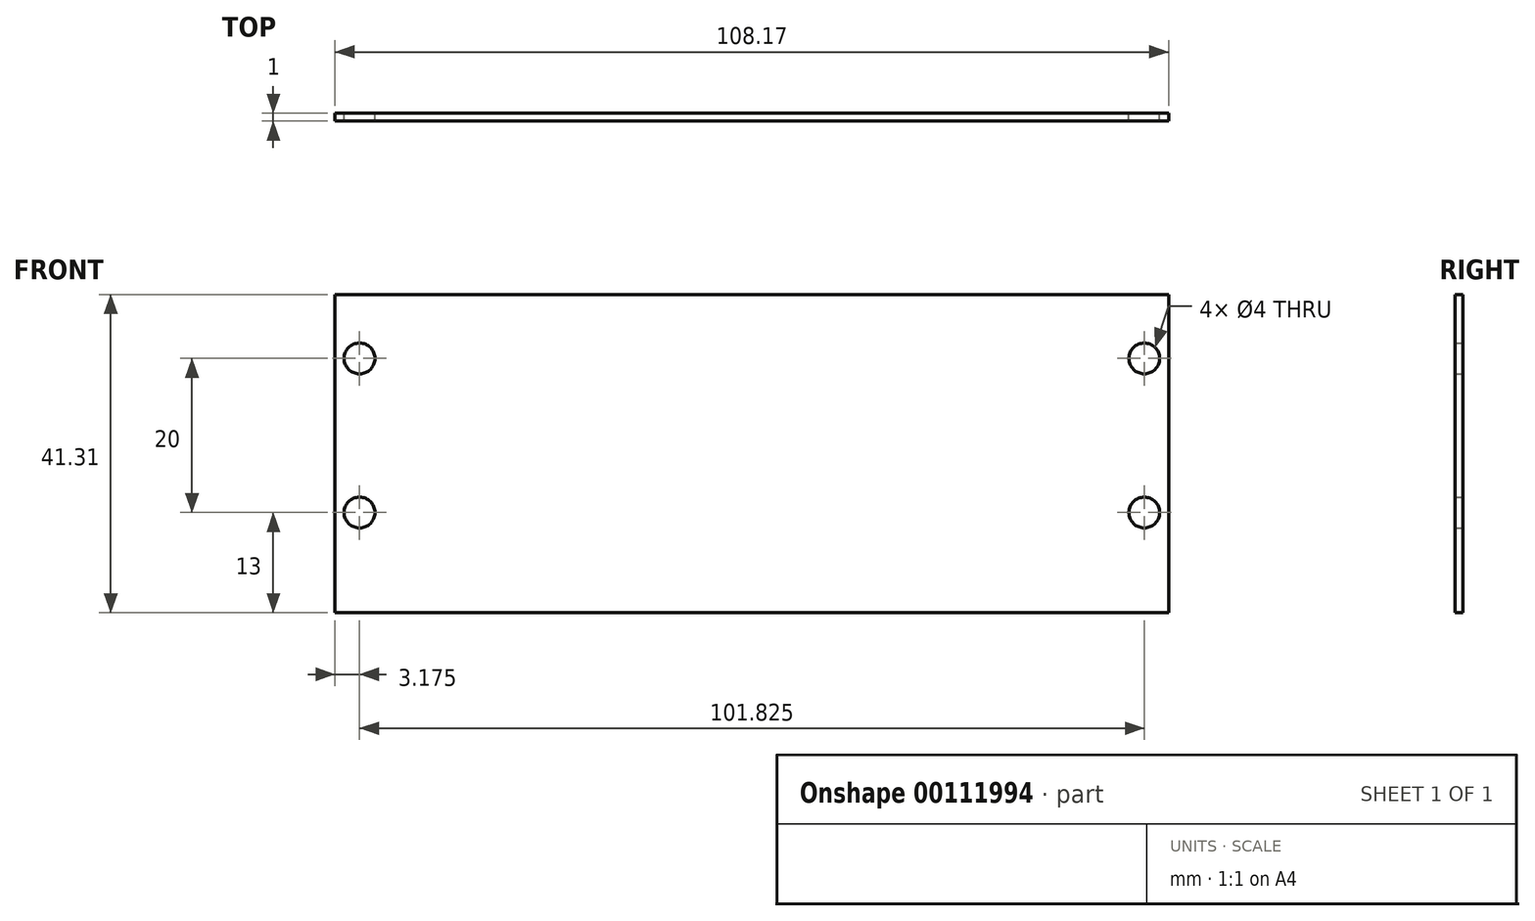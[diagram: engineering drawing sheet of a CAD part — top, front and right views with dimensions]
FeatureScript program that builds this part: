
annotation { "Feature Type Name" : "Feature", "Feature Type Description" : "" }
export const myFeature = defineFeature(function(context is Context, id is Id, definition is map)
    precondition{}
    {
        {
            var Q0;
            Q0=qCreatedBy(makeId("Front.planeOp"),FACE);
            var sketch = newSketch(context, id + "F0", { "sketchPlane" : qUnion([Q0])});
            skLineSegment(sketch, "E0.bottom", {"start": v(0, 0) * mm, "end": v(108.17, 0) * mm});
            skLineSegment(sketch, "E0.top", {"start": v(0, 41.31) * mm, "end": v(108.17, 41.31) * mm});
            skLineSegment(sketch, "E0.left", {"start": v(0, 0) * mm, "end": v(0, 41.31) * mm});
            skLineSegment(sketch, "E0.right", {"start": v(108.17, 0) * mm, "end": v(108.17, 41.31) * mm});
            skLineSegment(sketch, "E1.bottom", {"start": v(3.17, 33) * mm, "end": v(105, 33) * mm, "construction": true});
            skLineSegment(sketch, "E1.top", {"start": v(3.17, 13) * mm, "end": v(105, 13) * mm, "construction": true});
            skLineSegment(sketch, "E1.left", {"start": v(3.17, 33) * mm, "end": v(3.17, 13) * mm, "construction": true});
            skLineSegment(sketch, "E1.right", {"start": v(105, 33) * mm, "end": v(105, 13) * mm, "construction": true});
            skCircle(sketch, "E2", {"center": v(3.17, 33) * mm, "radius": 2 * mm});
            skCircle(sketch, "E3", {"center": v(3.17, 13) * mm, "radius": 2 * mm});
            skCircle(sketch, "E4", {"center": v(105, 13) * mm, "radius": 2 * mm});
            skCircle(sketch, "E5", {"center": v(105, 33) * mm, "radius": 2 * mm});
            skSolve(sketch);
        }
        {
            var Q0;
            Q0 = qSketchRegion(id + "F0", true);
            extrude(context, id + "F1", {"entities" : qUnion([Q0]), "depth" : 1 * mm});
        }
    });
